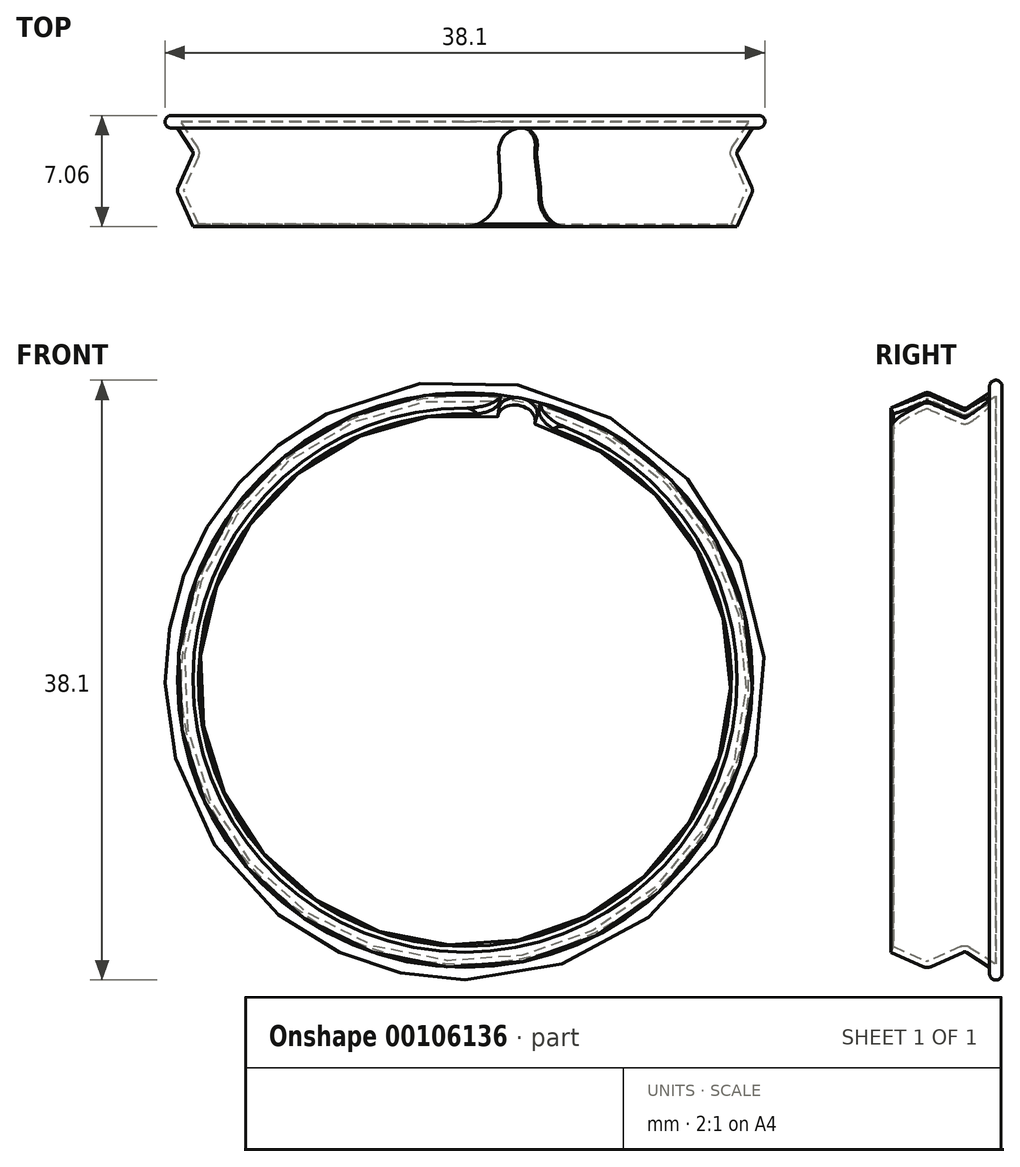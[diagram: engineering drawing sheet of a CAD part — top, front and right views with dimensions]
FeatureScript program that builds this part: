
annotation { "Feature Type Name" : "Feature", "Feature Type Description" : "" }
export const myFeature = defineFeature(function(context is Context, id is Id, definition is map)
    precondition{}
    {
        {
            var Q0;
            Q0=qCreatedBy(makeId("Right.planeOp"),FACE);
            var sketch = newSketch(context, id + "F0", { "sketchPlane" : qUnion([Q0])});
            skLineSegment(sketch, "E0", {"start": v(-152.4, 0) * mm, "end": v(152.4, 0) * mm, "construction": true});
            skLineSegment(sketch, "E1", {"start": v(153.2, 0) * mm, "end": v(153.2, 18.65) * mm});
            skLineSegment(sketch, "E2", {"start": v(153.2, 0) * mm, "end": v(152.8, 0) * mm});
            skLineSegment(sketch, "E3", {"start": v(152.8, 0) * mm, "end": v(152.8, 18.65) * mm});
            skArc(sketch, "E4", {"start": v(153.2, 18.65) * mm, "mid": v(152.8, 19.05) * mm, "end": v(152.4, 18.65) * mm});
            skLineSegment(sketch, "E5", {"start": v(152.4, 18.65) * mm, "end": v(152.4, 18.26) * mm});
            skArc(sketch, "E6", {"start": v(150.73, 17.28) * mm, "mid": v(150.83, 17.26) * mm, "end": v(150.92, 17.3) * mm});
            skArc(sketch, "E7", {"start": v(148.51, 17.84) * mm, "mid": v(148.43, 17.86) * mm, "end": v(148.35, 17.84) * mm});
            skArc(sketch, "E8", {"start": v(150.57, 16.92) * mm, "mid": v(150.86, 16.87) * mm, "end": v(151.14, 16.96) * mm});
            skArc(sketch, "E9", {"start": v(148.67, 18.2) * mm, "mid": v(148.43, 18.26) * mm, "end": v(148.19, 18.2) * mm});
            skLineSegment(sketch, "E10", {"start": v(152.4, 18.26) * mm, "end": v(150.92, 17.3) * mm});
            skLineSegment(sketch, "E11", {"start": v(150.92, 17.3) * mm, "end": v(151.14, 16.96) * mm, "construction": true});
            skLineSegment(sketch, "E12", {"start": v(151.14, 16.96) * mm, "end": v(152.8, 18.04) * mm});
            skLineSegment(sketch, "E13", {"start": v(150.73, 17.28) * mm, "end": v(148.67, 18.2) * mm});
            skLineSegment(sketch, "E14", {"start": v(150.73, 17.28) * mm, "end": v(150.57, 16.92) * mm, "construction": true});
            skLineSegment(sketch, "E15", {"start": v(148.67, 18.2) * mm, "end": v(148.51, 17.84) * mm, "construction": true});
            skLineSegment(sketch, "E16", {"start": v(148.51, 17.84) * mm, "end": v(150.57, 16.92) * mm});
            skLineSegment(sketch, "E17", {"start": v(148.43, 17.66) * mm, "end": v(148.43, 18.26) * mm, "construction": true});
            skLineSegment(sketch, "E18.MirrorCS", {"start": v(148.19, 18.2) * mm, "end": v(148.35, 17.84) * mm, "construction": true});
            skLineSegment(sketch, "E19.MirrorCS", {"start": v(148.35, 17.84) * mm, "end": v(146.3, 16.92) * mm});
            skLineSegment(sketch, "E20.MirrorCS", {"start": v(146.13, 17.28) * mm, "end": v(148.19, 18.2) * mm});
            skLineSegment(sketch, "E21", {"start": v(146.13, 17.28) * mm, "end": v(146.3, 16.92) * mm});
            skSolve(sketch);
        }
        {
            var Q0;
            Q0 = qSketchRegion(id + "F0", true);
            var Q1;
            Q1=sQuery(id+"F0.wireOp",EDGE,"E0");
            revolve(context, id + "F1", {"entities" : qUnion([Q0]), "axis" : qUnion([Q1]), "revolveType" : RevolveType.FULL});
        }
        {
            var Q0;
            Q0=qCreatedBy(makeId("Top.planeOp"),FACE);
            cPlane(context, id + "F2", {"entities" : qUnion([Q0]), "cplaneType" : CPlaneType.OFFSET, "offset" : 19.05 * mm, "width" : 152.4 * mm, "height" : 152.4 * mm});
        }
        {
            var Q0;
            Q0=qCreatedBy(makeId("Top.planeOp"),FACE);
            cPlane(context, id + "F3", {"entities" : qUnion([Q0]), "cplaneType" : CPlaneType.OFFSET, "offset" : 6.35 * mm, "width" : 152.4 * mm, "height" : 152.4 * mm});
        }
        {
            var Q0;
            Q0=qCreatedBy(id+"F2.planeOp",FACE);
            var sketch = newSketch(context, id + "F4", { "sketchPlane" : qUnion([Q0])});
            skLineSegment(sketch, "E22", {"start": v(0, 152.4) * mm, "end": v(0, 146.13) * mm, "construction": true});
            skLineSegment(sketch, "E23", {"start": v(3.79, 152.4) * mm, "end": v(3.79, 146.13) * mm, "construction": true});
            skPoint(sketch, "E24", {"position": v(3.79, 151.03) * mm});
            skPoint(sketch, "E25", {"position": v(0, 148.49) * mm});
            skLineSegment(sketch, "E26", {"start": v(2.38, 151.03) * mm, "end": v(2.38, 148.49) * mm});
            skEllipticalArc(sketch, "E27", {});
            skEllipticalArc(sketch, "E28", {});
            skEllipticalArc(sketch, "E29.MirrorCS", {});
            skLineSegment(sketch, "E30.MirrorCS", {"start": v(5.2, 151.03) * mm, "end": v(5.2, 148.49) * mm});
            skEllipticalArc(sketch, "E31.MirrorCS", {});
            skLineSegment(sketch, "E32", {"start": v(0, 146.13) * mm, "end": v(7.58, 146.13) * mm});
            const initialGuessF4  = {"E27": [0, 0.14848840000000002, 0, -1, 0.0023622000000000087, 0.00238252, 6.283185307179586, 1.5707963267948968], "E28": [0.0037896799999999997, 0.1510284, -1, 0, 0.0014071599999999993, 0.0013716000000000006, 4.71238898038469, 0], "E29.MirrorCS": [0.003789680000000001, 0.1510284, 1, 0, 0.0014071599999999993, 0.0013716000000000006, 0, 1.5707963267948968], "E31.MirrorCS": [0.007579360000000001, 0.14848840000000002, 0, -1, 0.0023622000000000087, 0.00238252, 4.71238898038469, 6.283185307179586]};
            skSetInitialGuess(sketch, initialGuessF4);
            skSolve(sketch);
        }
        {
            var Q0;
            Q0=qCreatedBy(id+"F3.planeOp",FACE);
            var sketch = newSketch(context, id + "F5", { "sketchPlane" : qUnion([Q0])});
            skLineSegment(sketch, "E33", {"start": v(0, 152.4) * mm, "end": v(0, 146.13) * mm, "construction": true});
            skLineSegment(sketch, "E34", {"start": v(1.26, 152.4) * mm, "end": v(1.26, 146.13) * mm, "construction": true});
            skPoint(sketch, "E35", {"position": v(1.26, 151.03) * mm});
            skPoint(sketch, "E36", {"position": v(0, 148.49) * mm});
            skLineSegment(sketch, "E37", {"start": v(0.8, 151.03) * mm, "end": v(0.8, 148.49) * mm});
            skEllipticalArc(sketch, "E38", {});
            skEllipticalArc(sketch, "E39", {});
            skEllipticalArc(sketch, "E40.MirrorCS", {});
            skLineSegment(sketch, "E41.MirrorCS", {"start": v(1.73, 151.03) * mm, "end": v(1.73, 148.49) * mm});
            skEllipticalArc(sketch, "E42.MirrorCS", {});
            skLineSegment(sketch, "E43", {"start": v(0, 146.13) * mm, "end": v(2.52, 146.13) * mm});
            const initialGuessF5  = {"E38": [0, 0.14848840000000002, 1, 0, 0.0007950200000000004, 0.0023622000000000087, 4.71238898038469, 6.283185307179586], "E39": [0.0012623800000000002, 0.1510284, -1, 0, 0.00046735999999999956, 0.0013716000000000006, 4.71238898038469, 6.283185307179586], "E40.MirrorCS": [0.00126238, 0.1510284, 1, 0, 0.00046735999999999956, 0.0013716000000000006, 6.283185307179586, 1.5707963267948966], "E42.MirrorCS": [0.0025247600000000005, 0.14848840000000002, -1, 0, 0.0007950200000000004, 0.0023622000000000087, 6.283185307179586, 1.5707963267948966]};
            skSetInitialGuess(sketch, initialGuessF5);
            skSolve(sketch);
        }
        {
            var Q1;
            Q1=makeQuery(id+"F4.imprint","IMPRINT",FACE,{"disambiguationData":[TD([[makeQuery(id+"F4.imprint","IMPRINT",EDGE,{"derivedFrom":sQuery(id+"F4.wireOp",EDGE,"E26")}),1.0]])]});
            var Q2;
            Q2=makeQuery(id+"F5.imprint","IMPRINT",FACE,{"disambiguationData":[TD([[makeQuery(id+"F5.imprint","IMPRINT",EDGE,{"derivedFrom":sQuery(id+"F5.wireOp",EDGE,"E37")}),1.0]])]});
            loft(context, id + "F6", {"operationType" : NewBodyOperationType.REMOVE, "sheetProfilesArray" : [{ "sheetProfileEntities" : qUnion([Q1]) }, { "sheetProfileEntities" : qUnion([Q2]) }]});
        }
    });
